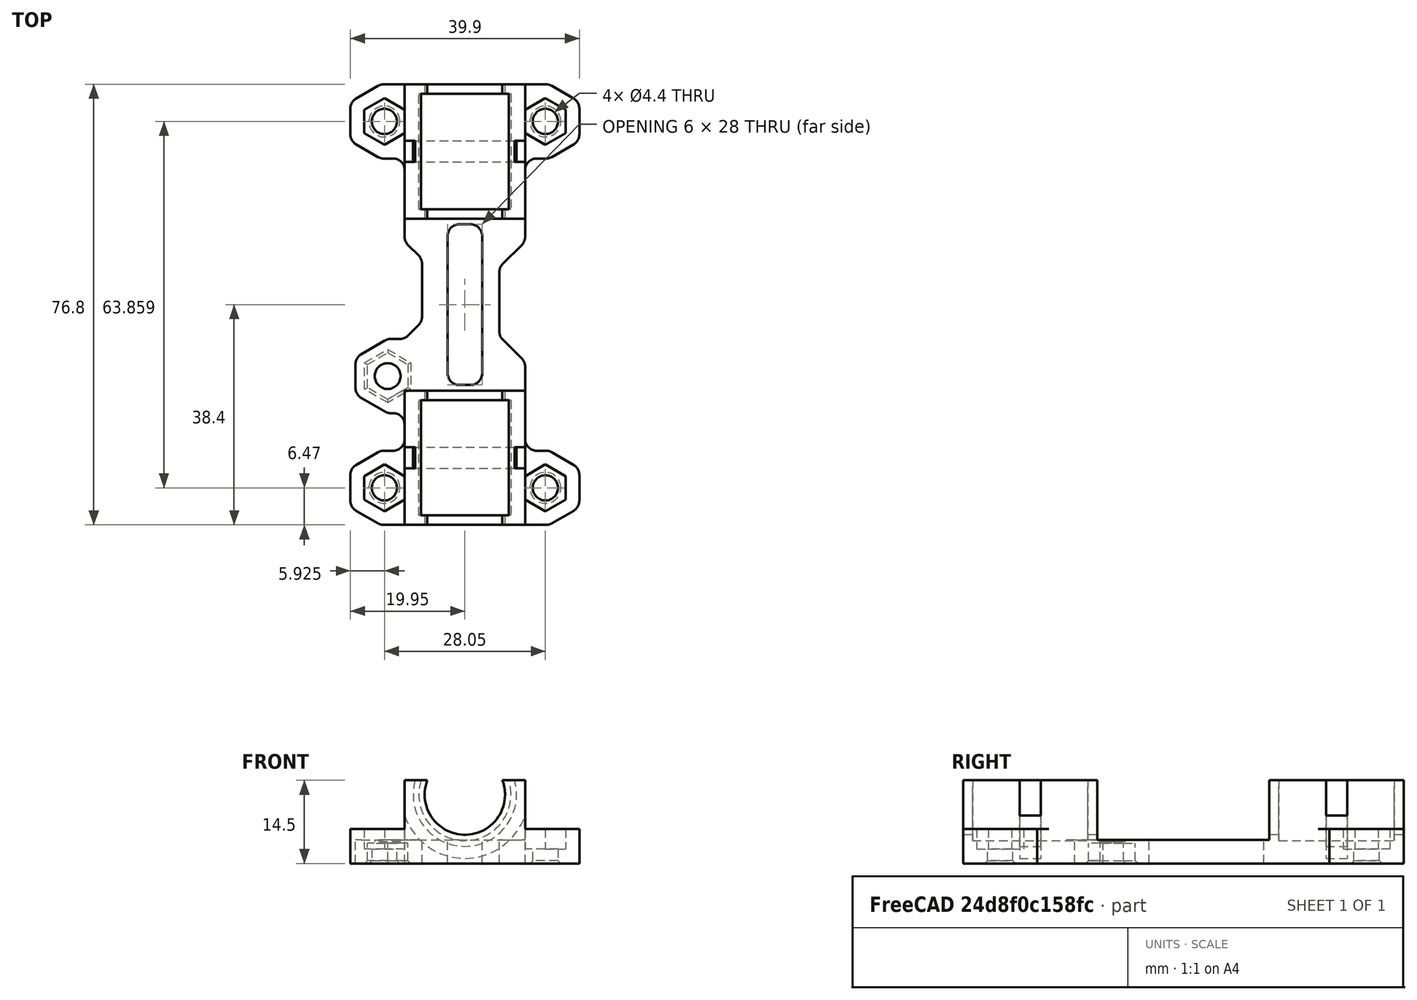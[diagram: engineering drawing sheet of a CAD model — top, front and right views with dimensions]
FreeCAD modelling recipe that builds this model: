
FCSTD DOCUMENT  (FreeCAD 0.15R4671 (Git))
Label: Halter Gleitlager Z - Zusammenbau links
License: All rights reserved
LicenseURL: http://de.wikipedia.org/wiki/Alle_Rechte_vorbehalten
objects: Part::FeaturePython×7, Part::MultiFuse×1, PartDesign::Chamfer×1, PartDesign::Fillet×1
note: 10 computed .brp shape members not serialized (recipe doc carries the construction recipe); baked Part::Feature solids carry a one-line shape summary decoded from their .brp

FEATURE [Part::FeaturePython] Halter_Gleitlager_Z___Zwischenstueck_01  # a2plus imported part (geometry in sourceFile) (typed FeaturePython)
  fixedPosition = true
  sourceFile = <path> Gleitlager Z - Zwischenstueck links.FCStd
  timeLastImport = 1.45546e+09
  updateColors = true
FEATURE [Part::FeaturePython] Halter_Gleitlager_Z___Gleitlager_01  # a2plus imported part (geometry in sourceFile) (typed FeaturePython)
  Placement = pos=(0,26.2,0) rot=(0,0,1;0rad)
  fixedPosition = false
  sourceFile = <path> Gleitlager Z - Gleitlager.FCStd
  timeLastImport = 1.45545e+09
  updateColors = true
FEATURE [Part::FeaturePython] Halter_Gleitlager_Z___Gleitlager_01001  # a2plus imported part (geometry in sourceFile) (typed FeaturePython)
  Placement = pos=(0,-27.2,0) rot=(0,0,1;0rad)
  fixedPosition = false
  sourceFile = <path> Gleitlager Z - Gleitlager.FCStd
  timeLastImport = 1.45545e+09
  updateColors = true
FEATURE [Part::FeaturePython] Halter_Gleitlager_Z___Verschraubung_01  # a2plus imported part (geometry in sourceFile) (typed FeaturePython)
  Placement = pos=(14.025,31.4297,0) rot=(0,0,1;0rad)
  fixedPosition = false
  sourceFile = <path> Gleitlager Z - Verschraubung.FCStd
  timeLastImport = 1.45539e+09
  updateColors = true
FEATURE [Part::FeaturePython] Halter_Gleitlager_Z___Verschraubung_01001  # a2plus imported part (geometry in sourceFile) (typed FeaturePython)
  Placement = pos=(14.025,-32.4297,0) rot=(0,0,1;0rad)
  fixedPosition = false
  sourceFile = <path> Gleitlager Z - Verschraubung.FCStd
  timeLastImport = 1.45539e+09
  updateColors = true
FEATURE [Part::FeaturePython] Halter_Gleitlager_Z___Verschraubung_  # a2plus imported part (geometry in sourceFile) (typed FeaturePython)
  Placement = pos=(-14.025,-32.4297,0) rot=(0,0,1;3.14159rad)
  fixedPosition = false
  sourceFile = <path> Gleitlager Z - Verschraubung.FCStd
  timeLastImport = 1.45539e+09
  updateColors = true
FEATURE [Part::FeaturePython] Halter_Gleitlager_Z___Verschraubung_01002  # a2plus imported part (geometry in sourceFile) (typed FeaturePython)
  Placement = pos=(-14.025,31.4297,0) rot=(0,0,1;3.14159rad)
  fixedPosition = false
  sourceFile = <path> Gleitlager Z - Verschraubung.FCStd
  timeLastImport = 1.45539e+09
  updateColors = true
FEATURE [Part::MultiFuse] Fusion
  Shapes = -> [Halter_Gleitlager_Z___Verschraubung_01002,Halter_Gleitlager_Z___Verschraubung_01001,Halter_Gleitlager_Z___Gleitlager_01001,Halter_Gleitlager_Z___Verschraubung_,Halter_Gleitlager_Z___Verschraubung_01,Halter_Gleitlager_Z___Gleitlager_01,Halter_Gleitlager_Z___Zwischenstueck_01]
FEATURE [PartDesign::Chamfer] Chamfer
  Base = -> Fusion [Edge145,Edge152,Edge181,Edge193,Edge30,Edge28,Edge26,Edge27,Edge29,Edge31]
  Size = 0.5
FEATURE [PartDesign::Fillet] Fillet
  Base = -> Chamfer [Edge334,Edge332,Edge284,Edge156,Edge69,Edge64,Edge50,Edge46,Edge43,Edge41,Edge276,Edge275,Edge244,Edge62,Edge58,Edge54,Edge134,Edge272,Edge91,Edge333,Edge86,Edge87,Edge241,Edge243,Edge242,Edge66,Edge75,Edge82,Edge190,Edge342,Edge343,Edge339,Edge202,Edge95,Edge71,Edge337,Edge89]
  Radius = 2
note: 7 file-system paths scrubbed to <path> (originals preserved in the JSON sidecar)
